# Revit family: SYSCOOL FLOOR 24 HP Q, наружный  блок
name_source: partatom
category: Оборудование
units: mm (PartAtom-declared; Revit-internal decimal feet)

## family parameters
Всегда вертикально = Да
Заголовок OmniClass = Climate Control (HVAC)
На основе рабочей плоскости = Нет
Номер OmniClass = 23.75.00.00
Общий = Нет
При загрузке вырезать с полостями = Нет
Размер круглого соединителя = Использовать диаметр
Тип детали = Нормальный
Точка расчета площади = Нет

## types (1)
- MOX430-24HN1-QB6
    Air Flow = 3650.00 м³/ч
    Casing color = SB2098
    Compressor = 1
    Depth = 342 мм
    Gas = R410A
    Gas pipe = 15.9 мм
    Gas pipe Radius = 7.95 мм
    Height = 673 мм
    Installation = Outdoor installation
    Liquid pipe = 9.52 мм
    Liquid pipe Radius = 4.76 мм
    Net Weight = 55.50 кг
    Power supply = 1 phase, 220-240V, 50Hz
    Width = 890 мм
    clearance access behind = 300 мм
    clearance access front = 2000 мм
    clearance access left = 300 мм
    clearance access right = 600 мм
    Группа модели = MOX430-24HN1-QB6

## geometry (parser evidence)
native form markers: Sweep x26
no freeform markers — native parametric forms only
